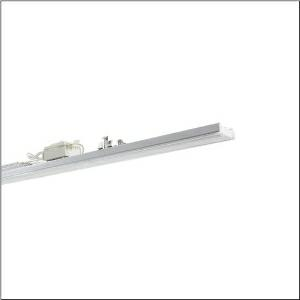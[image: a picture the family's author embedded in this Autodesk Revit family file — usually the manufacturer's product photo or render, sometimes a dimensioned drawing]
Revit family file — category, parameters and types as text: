
# Revit family: licross_11_recessed_ho_51te1edv4m1s
name_source: partatom
category: Lighting Fixtures
units: mm (PartAtom-declared; Revit-internal decimal feet)

## family parameters
Cut with Voids When Loaded = No
Host = Face
Light Source = No
Part Type = Normal
Room Calculation Point = No
Round Connector Dimension = Use Diameter
Shared = No

## types (1)
- --- (1 x LED, 26450 lm, 150.5 W, 4000K)
    Apparent Load = 150 VA
    CIE Flux Codes = 85 95 99 100 100
    Color Rendering = 80
    Color Temperature = 4000K
    Default Elevation = 1800 mm
    Description = Licross 11 Recessed HO, luminaire insert, of sheet steel, galvanised, coil coated, white, length: 2.250mm, width: 66mm, height: 67mm, LED rated luminous flux: 26.450lm, light colour: 840, SDCM (Standard Deviation of Colour Matching)MacAdam ≤ 2 SDCM (initial), control gear: DALI 2, with plug, 5-pole, with phase selection, mains connection: 220..240V, AC, 50/60Hz, rated input power: 151W, internal wiring halogen-free, primary light control with lens, of plastic, primary optical cover: cover, of PMMA, light emission: direct distribution, primary light characteristic: symmetric, protection rating (complete): IP54, insulation class (complete): insulation class I (protective earthing), certification: CE, ENEC, VDE, UKCA, protection symbol: D if used in an environment with non-conductive dust loads with corresponding accessories, impact resistance: IK06, permissible ambient temperature for indoor applications: -40..+35°C, corresponds to IFS (International Featured Standards) requirements for safety and quality in the food industry, reducing of maximum allowable ambient temperature of 5°C with ceiling mounting, LABS conformity tested according to VDMA 24364:2018-05, The light source and the operating device comply with the requirements of the Ecodesign Regulation (EU) 2019/2020 and are replaceable in accordance with this regulation, packaging unit: 1 piece
    Height = 58 mm
    Lamp = 1 x LED
    Lamp Light Flux = 26450 lm
    Lamp Power = 150.5 W
    Lamp count = 1
    Length = 2250 mm
    Luminous efficacy = 176 lm/W
    Manufacturer = Siteco
    ModVariant = No
    Model = 51TE1EDV4M1S
    Mounting Place = Ceiling
    Mounting Type = Pendant
    Number of Poles = 1
    OnlyDefault = Yes
    Power Factor = 1
    Product Name = Licross 11 Recessed HO
    Product group = luminaire insert | ceiling pendant
    ProductGroupID = 901
    Protection Class = Protection class I
    Protection Degree = IP 54
    RLX_Detail_Level = 1
    RLX_Emergency_Light_Flux = 0 lm
    RLX_Emergency_Type = 0
    RLX_Emergency_Type_DB = No
    RlxData = <blob elided: 30057 chars, md5=3a3c6032>
    Socket = socket
    Standby Power = 0 W
    System Light Flux = 26450 lm
    System Power = 150 W
    Type Comments = factory setting: luminous flux: 100 % | dim-lin: 254 | 690 mA
    Type Image = l_1296930.jpg
    URL = http://relux.com
    VarID = @adj_099519
    Voltage = 0 V
    Weight = 0.00 kg
    Width = 66 mm

## geometry (parser evidence)
native form markers: Blend x4, Sweep x10
no freeform markers — native parametric forms only
